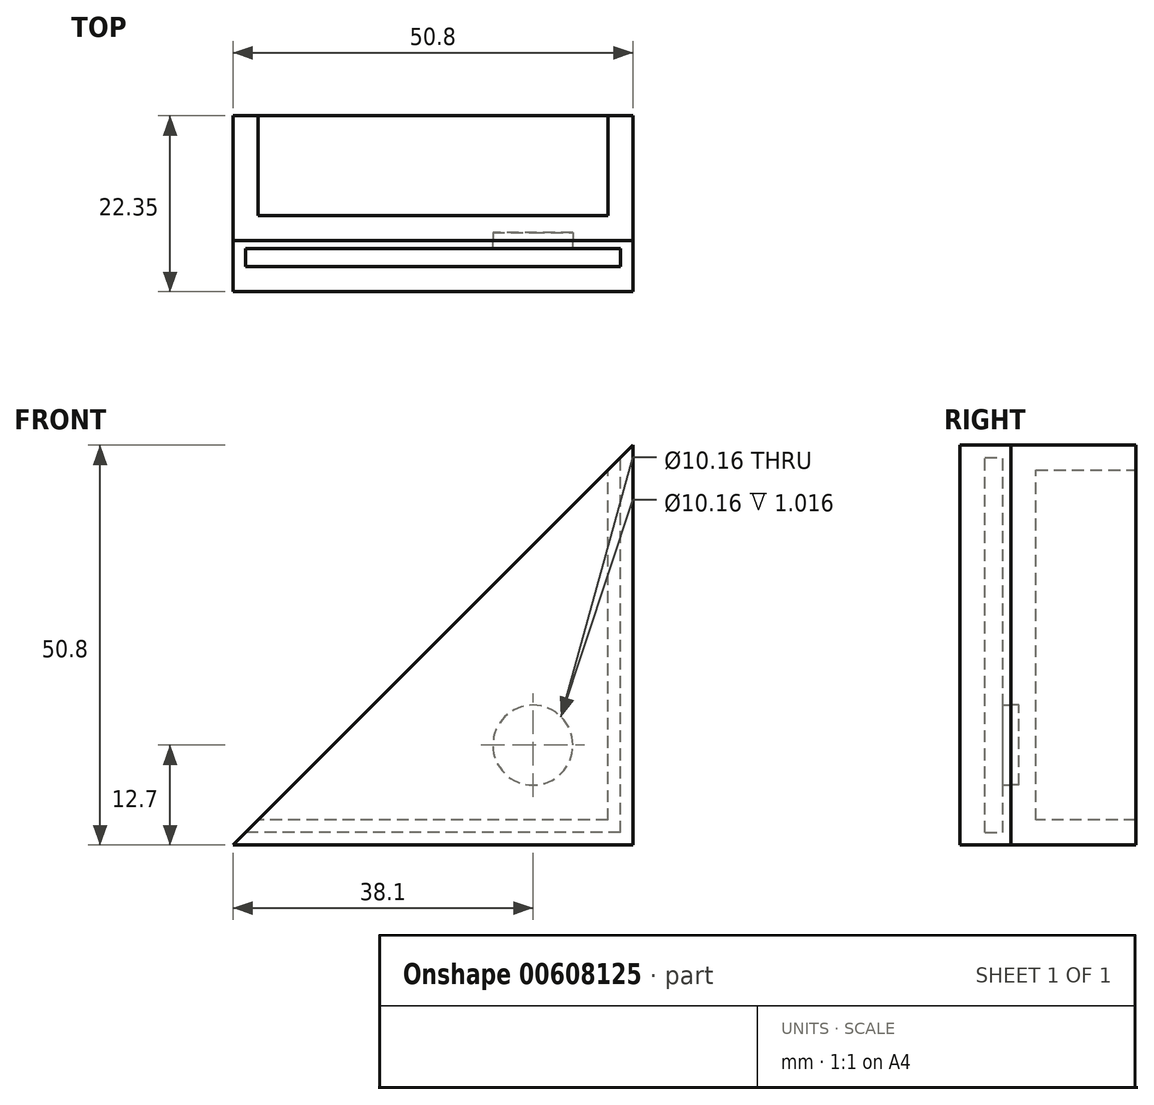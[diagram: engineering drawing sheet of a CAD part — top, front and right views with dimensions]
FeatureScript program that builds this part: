
annotation { "Feature Type Name" : "Feature", "Feature Type Description" : "" }
export const myFeature = defineFeature(function(context is Context, id is Id, definition is map)
    precondition{}
    {
        {
            var Q0;
            Q0=qCreatedBy(makeId("Front.planeOp"),FACE);
            var sketch = newSketch(context, id + "F0", { "sketchPlane" : qUnion([Q0])});
            skLineSegment(sketch, "E0.bottom", {"start": v(0, 0) * mm, "end": v(-50.8, 0) * mm});
            skLineSegment(sketch, "E0.left", {"start": v(0, 0) * mm, "end": v(0, 50.8) * mm});
            skLineSegment(sketch, "E1", {"start": v(-50.8, 0) * mm, "end": v(0, 50.8) * mm});
            skSolve(sketch);
        }
        {
            var Q0;
            Q0=makeQuery(id+"F0.imprint","IMPRINT",FACE,{"disambiguationData":[TD([[makeQuery(id+"F0.imprint","IMPRINT",EDGE,{"derivedFrom":sQuery(id+"F0.wireOp",EDGE,"E0.bottom")}),-1.0]])]});
            extrude(context, id + "F1", {"entities" : qUnion([Q0]), "depth" : 3.17 * mm, "offsetDistance" : 25.4 * mm});
        }
        {
            var Q0;
            Q0=makeQuery(id+"F1.opExtrude","CAP_FACE",FACE,{"disambiguationData":[OSD([sQuery(id+"F0.wireOp",EDGE,"E0.bottom"),sQuery(id+"F0.wireOp",EDGE,"E0.left"),sQuery(id+"F0.wireOp",EDGE,"E1")])],"isStart":false});
            var sketch = newSketch(context, id + "F2", { "sketchPlane" : qUnion([Q0])});
            skCircle(sketch, "E2", {"center": v(-12.7, 12.7) * mm, "radius": 5.08 * mm});
            skSolve(sketch);
        }
        {
            var Q0;
            Q0=qSketchRegion(id+"F2",true);
            extrude(context, id + "F3", {"entities" : qUnion([Q0]), "operationType" : NewBodyOperationType.REMOVE, "oppositeDirection" : true, "depth" : 1.02 * mm, "offsetDistance" : 25.4 * mm});
        }
        {
            var Q0;
            Q0=makeQuery(id+"F1.opExtrude","SWEPT_FACE",FACE,{"disambiguationData":[OSD([sQuery(id+"F0.wireOp",EDGE,"E0.bottom")])]});
            var sketch = newSketch(context, id + "F4", { "sketchPlane" : qUnion([Q0])});
            skLineSegment(sketch, "E3.bottom", {"start": v(0, 0) * mm, "end": v(-50.8, 0) * mm});
            skLineSegment(sketch, "E3.top", {"start": v(0, -12.7) * mm, "end": v(-50.8, -12.7) * mm});
            skLineSegment(sketch, "E3.left", {"start": v(0, 0) * mm, "end": v(0, -12.7) * mm});
            skLineSegment(sketch, "E3.right", {"start": v(-50.8, 0) * mm, "end": v(-50.8, -12.7) * mm});
            skSolve(sketch);
        }
        {
            var Q0;
            Q0=makeQuery(id+"F4.imprint","IMPRINT",FACE,{"disambiguationData":[TD([[makeQuery(id+"F4.imprint","IMPRINT",EDGE,{"derivedFrom":sQuery(id+"F4.wireOp",EDGE,"E3.bottom")}),1.0]])]});
            extrude(context, id + "F5", {"entities" : qUnion([Q0]), "oppositeDirection" : true, "depth" : 3.17 * mm, "offsetDistance" : 25.4 * mm});
        }
        {
            var Q0;
            Q0=makeQuery(id+"F1.opExtrude","SWEPT_FACE",FACE,{"disambiguationData":[OSD([sQuery(id+"F0.wireOp",EDGE,"E0.left")])]});
            var sketch = newSketch(context, id + "F6", { "sketchPlane" : qUnion([Q0])});
            skLineSegment(sketch, "E4.bottom", {"start": v(0, 50.8) * mm, "end": v(12.7, 50.8) * mm});
            skLineSegment(sketch, "E4.top", {"start": v(0, 0) * mm, "end": v(12.7, 0) * mm});
            skLineSegment(sketch, "E4.left", {"start": v(0, 50.8) * mm, "end": v(0, 0) * mm});
            skLineSegment(sketch, "E4.right", {"start": v(12.7, 50.8) * mm, "end": v(12.7, 0) * mm});
            skSolve(sketch);
        }
        {
            var Q0;
            Q0=makeQuery(id+"F6.imprint","IMPRINT",FACE,{"disambiguationData":[TD([[makeQuery(id+"F6.imprint","IMPRINT",EDGE,{"derivedFrom":sQuery(id+"F6.wireOp",EDGE,"E4.bottom")}),-1.0]])]});
            extrude(context, id + "F7", {"entities" : qUnion([Q0]), "operationType" : NewBodyOperationType.ADD, "oppositeDirection" : true, "depth" : 3.17 * mm, "offsetDistance" : 25.4 * mm});
        }
        {
            var Q0;
            Q0=makeQuery(id+"F7.boolean.opBoolean","MERGE",FACE,{"disambiguationData":[OD(0.0)],"derivedFrom":[makeQuery(id+"F5.opExtrude","SWEPT_FACE",FACE,{"disambiguationData":[OSD([sQuery(id+"F4.wireOp",EDGE,"E3.bottom")])]}),makeQuery(id+"F7.opExtrude","SWEPT_FACE",FACE,{"disambiguationData":[OSD([sQuery(id+"F6.wireOp",EDGE,"E4.left")])]})]});
            extrude(context, id + "F8", {"entities" : qUnion([Q0]), "operationType" : NewBodyOperationType.REMOVE, "endBound" : BoundingType.SYMMETRIC, "oppositeDirection" : true, "depth" : 25.4 * mm, "offsetDistance" : 25.4 * mm});
        }
        {
            var Q0;
            Q0=makeQuery(id+"F7.boolean.opBoolean","MERGE",FACE,{"disambiguationData":[OD(1.0)],"derivedFrom":[makeQuery(id+"F5.opExtrude","SWEPT_FACE",FACE,{"disambiguationData":[OSD([sQuery(id+"F4.wireOp",EDGE,"E3.bottom")])]}),makeQuery(id+"F7.opExtrude","SWEPT_FACE",FACE,{"disambiguationData":[OSD([sQuery(id+"F6.wireOp",EDGE,"E4.left")])]})]});
            extrude(context, id + "F9", {"entities" : qUnion([Q0]), "operationType" : NewBodyOperationType.REMOVE, "endBound" : BoundingType.SYMMETRIC, "depth" : 25.4 * mm, "offsetDistance" : 25.4 * mm});
        }
        {
            var Q0;
            Q0=makeQuery(id+"F1.opExtrude","CAP_FACE",FACE,{"disambiguationData":[OSD([sQuery(id+"F0.wireOp",EDGE,"E0.bottom"),sQuery(id+"F0.wireOp",EDGE,"E0.left"),sQuery(id+"F0.wireOp",EDGE,"E1")])],"isStart":false});
            var sketch = newSketch(context, id + "F10", { "sketchPlane" : qUnion([Q0])});
            skLineSegment(sketch, "E5", {"start": v(0, 0) * mm, "end": v(0, 50.8) * mm});
            skLineSegment(sketch, "E6", {"start": v(0, 50.8) * mm, "end": v(-50.8, 0) * mm});
            skLineSegment(sketch, "E7", {"start": v(-50.8, 0) * mm, "end": v(0, 0) * mm});
            skSolve(sketch);
        }
        {
            var Q0;
            Q0=makeQuery(id+"F10.imprint","IMPRINT",FACE,{"disambiguationData":[TD([[makeQuery(id+"F10.imprint","IMPRINT",EDGE,{"derivedFrom":sQuery(id+"F10.wireOp",EDGE,"E5")}),1.0]])]});
            extrude(context, id + "F11", {"entities" : qUnion([Q0]), "depth" : 1.02 * mm, "offsetDistance" : 25.4 * mm});
        }
        {
            var Q0;
            Q0=makeQuery(id+"F11.opExtrude","CAP_FACE",FACE,{"disambiguationData":[OSD([sQuery(id+"F2.wireOp",EDGE,"E2"),sQuery(id+"F10.wireOp",EDGE,"E5"),sQuery(id+"F10.wireOp",EDGE,"E6"),sQuery(id+"F10.wireOp",EDGE,"E7")])],"isStart":false});
            var sketch = newSketch(context, id + "F12", { "sketchPlane" : qUnion([Q0])});
            skLineSegment(sketch, "E8", {"start": v(-50.8, 0) * mm, "end": v(0, 0) * mm});
            skLineSegment(sketch, "E9", {"start": v(0, 0) * mm, "end": v(0, 50.8) * mm});
            skLineSegment(sketch, "E10", {"start": v(-1.59, 0) * mm, "end": v(-1.59, 49.21) * mm});
            skLineSegment(sketch, "E11", {"start": v(-1.59, 49.21) * mm, "end": v(0, 50.8) * mm});
            skLineSegment(sketch, "E12", {"start": v(0, 1.59) * mm, "end": v(-49.21, 1.59) * mm});
            skLineSegment(sketch, "E13", {"start": v(-49.21, 1.59) * mm, "end": v(-50.8, 0) * mm});
            skSolve(sketch);
        }
        {
            var Q0;
            {var subQ0=sQuery(id+"F12.wireOp",EDGE,"E13");Q0=makeQuery(id+"F12.imprint","IMPRINT",FACE,{"disambiguationData":[TD([[makeQuery(id+"F12.imprint","IMPRINT",EDGE,{"derivedFrom":subQ0}),-1.0]])]});}
            var Q1;
            {var subQ0=sQuery(id+"F12.wireOp",EDGE,"E9");var subQ1=sQuery(id+"F12.wireOp",EDGE,"E8");var subQ2=makeQuery(id+"F12.imprint","INTERSECT",VERTEX,{"derivedFrom":[subQ1,subQ0]});Q1=makeQuery(id+"F12.imprint","IMPRINT",FACE,{"disambiguationData":[TD([[makeQuery(id+"F12.imprint","IMPRINT",EDGE,{"disambiguationData":[TD([[subQ2,-1.0]])],"derivedFrom":subQ1}),-1.0]])]});}
            var Q2;
            {var subQ0=sQuery(id+"F12.wireOp",EDGE,"E11");Q2=makeQuery(id+"F12.imprint","IMPRINT",FACE,{"disambiguationData":[TD([[makeQuery(id+"F12.imprint","IMPRINT",EDGE,{"derivedFrom":subQ0}),-1.0]])]});}
            var Q3;
            Q3=sQuery(id+"F12.wireOp",EDGE,"E8");
            var Q4;
            Q4=sQuery(id+"F12.wireOp",EDGE,"E12");
            var Q5;
            Q5=sQuery(id+"F12.wireOp",EDGE,"E13");
            var Q6;
            Q6=sQuery(id+"F12.wireOp",EDGE,"E9");
            var Q7;
            Q7=sQuery(id+"F12.wireOp",EDGE,"E10");
            var Q8;
            Q8=sQuery(id+"F12.wireOp",EDGE,"E11");
            extrude(context, id + "F13", {"entities" : qUnion([Q0, Q1, Q2]), "operationType" : NewBodyOperationType.ADD, "surfaceEntities" : qUnion([Q3, Q4, Q5, Q6, Q7, Q8]), "depth" : 2.3 * mm, "offsetDistance" : 25.4 * mm});
        }
        {
            var Q0;
            Q0=makeQuery(id+"F13.opExtrude","CAP_FACE",FACE,{"disambiguationData":[OSD([sQuery(id+"F12.wireOp",EDGE,"E8"),sQuery(id+"F12.wireOp",EDGE,"E9"),sQuery(id+"F12.wireOp",EDGE,"E10"),sQuery(id+"F12.wireOp",EDGE,"E11"),sQuery(id+"F12.wireOp",EDGE,"E12"),sQuery(id+"F12.wireOp",EDGE,"E13")])],"isStart":false});
            var sketch = newSketch(context, id + "F14", { "sketchPlane" : qUnion([Q0])});
            skLineSegment(sketch, "E14", {"start": v(0, 0) * mm, "end": v(-50.8, 0) * mm});
            skLineSegment(sketch, "E15", {"start": v(-50.8, 0) * mm, "end": v(0, 50.8) * mm});
            skLineSegment(sketch, "E16", {"start": v(0, 50.8) * mm, "end": v(0, 0) * mm});
            skSolve(sketch);
        }
        {
            var Q0;
            {var subQ3=sQuery(id+"F14.wireOp",EDGE,"E14");Q0=makeQuery(id+"F14.imprint","IMPRINT",FACE,{"disambiguationData":[TD([[makeQuery(id+"F14.imprint","IMPRINT",EDGE,{"derivedFrom":subQ3}),-1.0]])]});}
            var Q1;
            {var subQ1=makeQuery(id+"F13.opExtrude","CAP_EDGE",EDGE,{"disambiguationData":[OSD([sQuery(id+"F12.wireOp",EDGE,"E10")])],"isStart":false});Q1=makeQuery(id+"F14.imprint","IMPRINT",FACE,{"disambiguationData":[TD([[makeQuery(id+"F14.imprint","IMPRINT",EDGE,{"derivedFrom":subQ1}),1.0]])]});}
            extrude(context, id + "F15", {"entities" : qUnion([Q0, Q1]), "operationType" : NewBodyOperationType.ADD, "depth" : 3.17 * mm, "offsetDistance" : 25.4 * mm});
        }
    });
